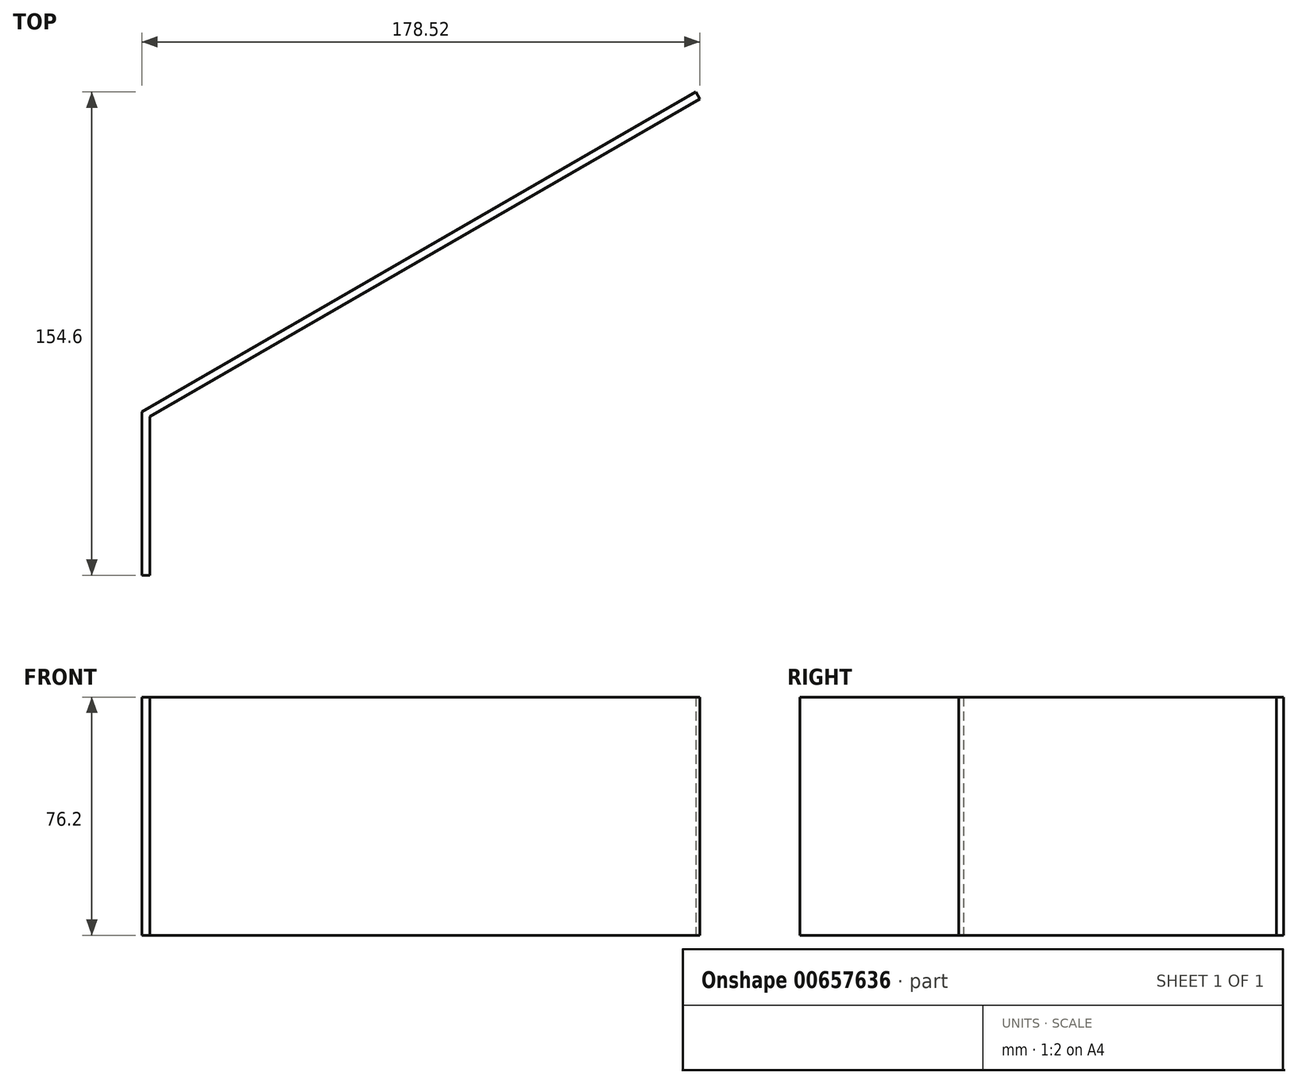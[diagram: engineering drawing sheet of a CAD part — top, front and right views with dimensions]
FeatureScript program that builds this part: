
annotation { "Feature Type Name" : "Feature", "Feature Type Description" : "" }
export const myFeature = defineFeature(function(context is Context, id is Id, definition is map)
    precondition{}
    {
        {
            var Q0;
            Q0=qCreatedBy(makeId("Top.planeOp"),FACE);
            var sketch = newSketch(context, id + "F0", { "sketchPlane" : qUnion([Q0])});
            skLineSegment(sketch, "E0.bottom", {"start": v(0, 0) * mm, "end": v(2.54, 0) * mm});
            skLineSegment(sketch, "E0.top", {"start": v(0, 50.8) * mm, "end": v(2.54, 50.8) * mm});
            skLineSegment(sketch, "E0.left", {"start": v(0, 0) * mm, "end": v(0, 50.8) * mm});
            skLineSegment(sketch, "E0.right", {"start": v(2.54, 0) * mm, "end": v(2.54, 50.8) * mm});
            skLineSegment(sketch, "E1", {"start": v(2.54, 50.8) * mm, "end": v(178.52, 152.4) * mm});
            skLineSegment(sketch, "E2", {"start": v(178.52, 152.4) * mm, "end": v(177.25, 154.6) * mm});
            skLineSegment(sketch, "E3", {"start": v(177.25, 154.6) * mm, "end": v(0, 52.27) * mm});
            skLineSegment(sketch, "E4", {"start": v(0, 52.27) * mm, "end": v(0, 50.8) * mm});
            skSolve(sketch);
        }
        {
            var Q0;
            Q0=makeQuery(id+"F0.imprint","IMPRINT",FACE,{"disambiguationData":[TD([[makeQuery(id+"F0.imprint","IMPRINT",EDGE,{"derivedFrom":sQuery(id+"F0.wireOp",EDGE,"E0.top")}),1.0]])]});
            var Q1;
            Q1=makeQuery(id+"F0.imprint","IMPRINT",FACE,{"disambiguationData":[TD([[makeQuery(id+"F0.imprint","IMPRINT",EDGE,{"derivedFrom":sQuery(id+"F0.wireOp",EDGE,"E0.bottom")}),1.0]])]});
            extrude(context, id + "F1", {"entities" : qUnion([Q0, Q1]), "depth" : 76.2 * mm, "offsetDistance" : 25.4 * mm});
        }
    });
